# Revit family: ledwaterproof_se-p_l1250-45w-840-ip69k_543022021200
name_source: partatom
category: Leuchten
revit_build: Autodesk Revit 2016 (Build: 20190508_0715(x64)
units: mm (PartAtom-declared; Revit-internal decimal feet)

## family parameters
Basisbauteil = Fläche
Beim Laden mit Abzugskörper schneiden = Nein
Bemaßung runder Anschluss = Durchmesser verwenden
Gemeinsam genutzt = Nein
Lichtquelle = Nein
Raumberechnungspunkt = Nein
Teiletyp = Normal

## types (1)
- LEDWaterproof SE-P L1250-45W-840-IP69K (1 x LED, 5850 lm)
    Approval mark = CE
    Beschreibung = Tubular waterproof luminaire with extra high IP rating. Suitable for outdoor application thanks to IP67/IP69K rating. Ammonium-resistant, suitable for livestock applications. Comfortable homogeneous light distribution. Easy installation due to free to position stainless steel mounting brackets. Equipped with 3x2.5mm² throughwiring.
    CIE Flux Codes = 42 72 90 89 100
    Control Gear = Electronic ballast
    Height = 73 mm
    Hersteller = OPPLE
    Lamp Light Flux = 5850 lm
    Lamp count = 1
    Lampe = 1 x LED
    Length = 1200 mm
    Luminous efficacy = 130 lm/W
    ModVariant = Nein
    Modell = 543022021200
    Mounting Place = Ceiling
    Mounting Type = Surface mounted
    Number of Poles = 1
    OnlyDefault = Ja
    Power Factor = 1
    Product Name = LEDWaterproof SE-P L1250-45W-840-IP69K
    Product group = Waterproof Special
    ProductGroupID = 350
    Protection Class = Protection class I
    Protection Degree = IP 65
    RLX_Detail_Level = 1
    RlxData = <blob elided: 117321 chars, md5=14f2eabf>
    Scheinlast = 45 VA
    Socket = socket
    Standby Power = 0 W
    System Light Flux = 5850 lm
    System Power = 45 W
    Typenbild = 543022021200.jpg
    Typenkommentare = Product without accessories
    URL = http://relux.com
    VarID = ---
    Voltage = 0 V
    Vorgabe-Ansicht = 1800 mm
    Weight = 0.00 kg
    Width = 73 mm

## geometry (parser evidence)
native form markers: Blend x4, Sweep x14
no freeform markers — native parametric forms only
